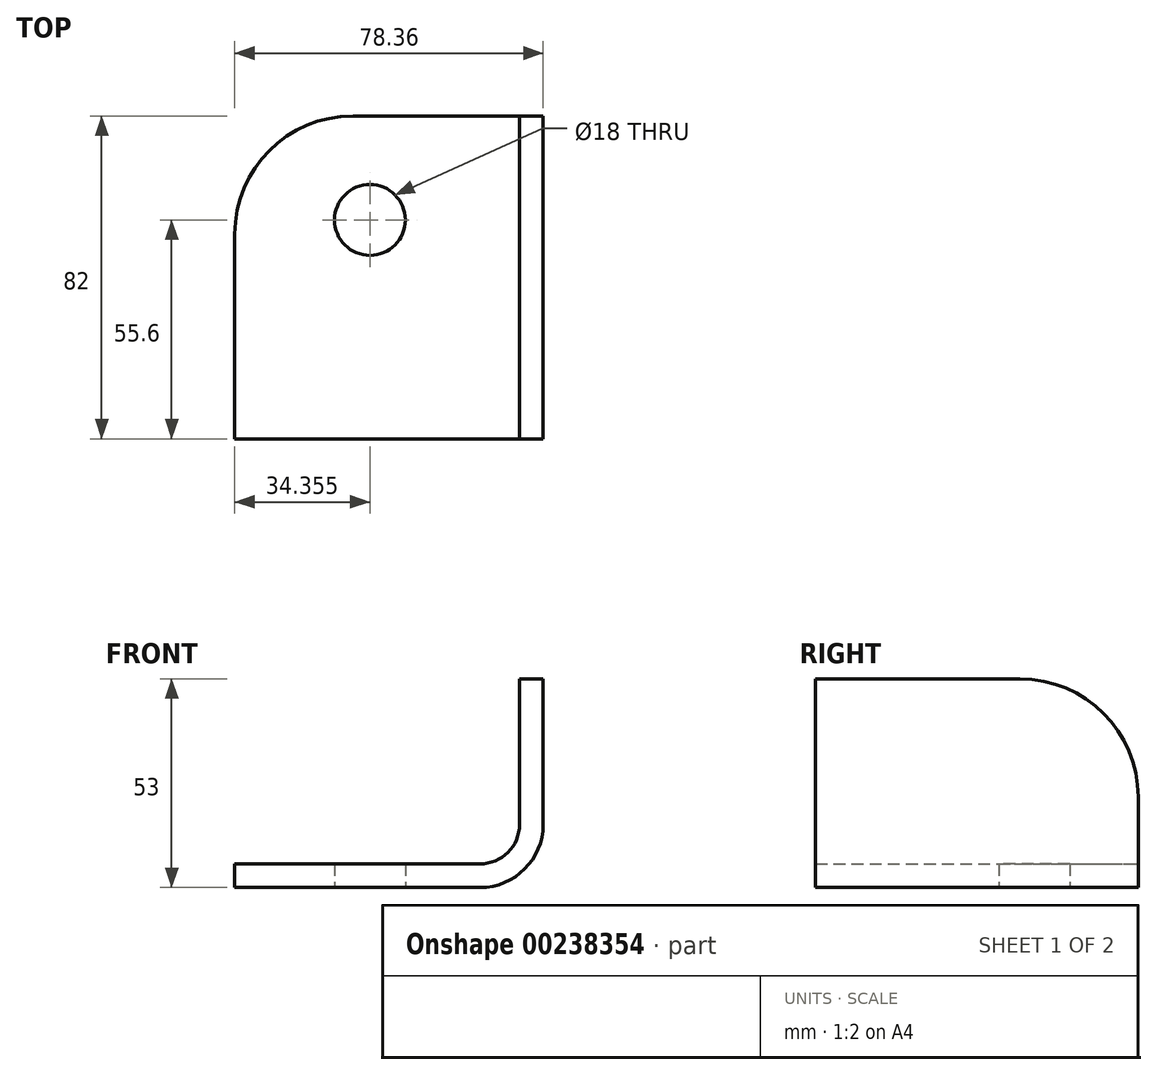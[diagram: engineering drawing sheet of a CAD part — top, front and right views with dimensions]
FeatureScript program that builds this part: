
annotation { "Feature Type Name" : "Feature", "Feature Type Description" : "" }
export const myFeature = defineFeature(function(context is Context, id is Id, definition is map)
    precondition{}
    {
        {
            var Q0;
            Q0=qCreatedBy(makeId("Front.planeOp"),FACE);
            var sketch = newSketch(context, id + "F0", { "sketchPlane" : qUnion([Q0])});
            skLineSegment(sketch, "E0", {"start": v(-58.04, -15.24) * mm, "end": v(4.32, -15.24) * mm});
            skLineSegment(sketch, "E1", {"start": v(20.32, 0.76) * mm, "end": v(20.32, 37.76) * mm});
            skLineSegment(sketch, "E2", {"start": v(20.32, 37.76) * mm, "end": v(14.32, 37.76) * mm});
            skLineSegment(sketch, "E3", {"start": v(14.32, 37.76) * mm, "end": v(14.32, 0.76) * mm});
            skLineSegment(sketch, "E4", {"start": v(4.32, -9.24) * mm, "end": v(-58.04, -9.24) * mm});
            skLineSegment(sketch, "E5", {"start": v(-58.04, -9.24) * mm, "end": v(-58.04, -15.24) * mm});
            skPoint(sketch, "E6.visualSharp", {"position": v(14.32, -9.24) * mm});
            skArc(sketch, "E6.filletArc", {"start": v(4.32, -9.24) * mm, "mid": v(11.39, -6.32) * mm, "end": v(14.32, 0.76) * mm});
            skPoint(sketch, "E7.visualSharp", {"position": v(20.32, -15.24) * mm});
            skArc(sketch, "E7.filletArc", {"start": v(4.32, -15.24) * mm, "mid": v(15.63, -10.56) * mm, "end": v(20.32, 0.76) * mm});
            skSolve(sketch);
        }
        {
            var Q0;
            Q0 = qSketchRegion(id + "F0", true);
            extrude(context, id + "F1", {"entities" : qUnion([Q0]), "depth" : 82 * mm});
        }
        {
            var Q0;
            Q0=makeQuery(id+"F1.opExtrude","SWEPT_FACE",FACE,{"disambiguationData":[OSD([sQuery(id+"F0.wireOp",EDGE,"E0")])]});
            var sketch = newSketch(context, id + "F2", { "sketchPlane" : qUnion([Q0])});
            skCircle(sketch, "E8", {"center": v(-23.68, 26.4) * mm, "radius": 9 * mm});
            skSolve(sketch);
        }
        {
            var Q0;
            Q0 = qSketchRegion(id + "F2", true);
            extrude(context, id + "F3", {"entities" : qUnion([Q0]), "operationType" : NewBodyOperationType.REMOVE, "oppositeDirection" : true, "depth" : 25 * mm});
        }
        {
            var Q0;
            Q0=makeQuery(id+"F1.opExtrude","CAP_EDGE",EDGE,{"disambiguationData":[OSD([sQuery(id+"F0.wireOp",EDGE,"E5")])],"isStart":true});
            var Q1;
            Q1=makeQuery(id+"F1.opExtrude","CAP_EDGE",EDGE,{"disambiguationData":[OSD([sQuery(id+"F0.wireOp",EDGE,"E2")])],"isStart":true});
            fillet(context, id + "F4", {"entities" : qUnion([Q0, Q1]), "radius" : 30 * mm, "tangentPropagation" : true, "allowEdgeOverflow" : false});
        }
    });
